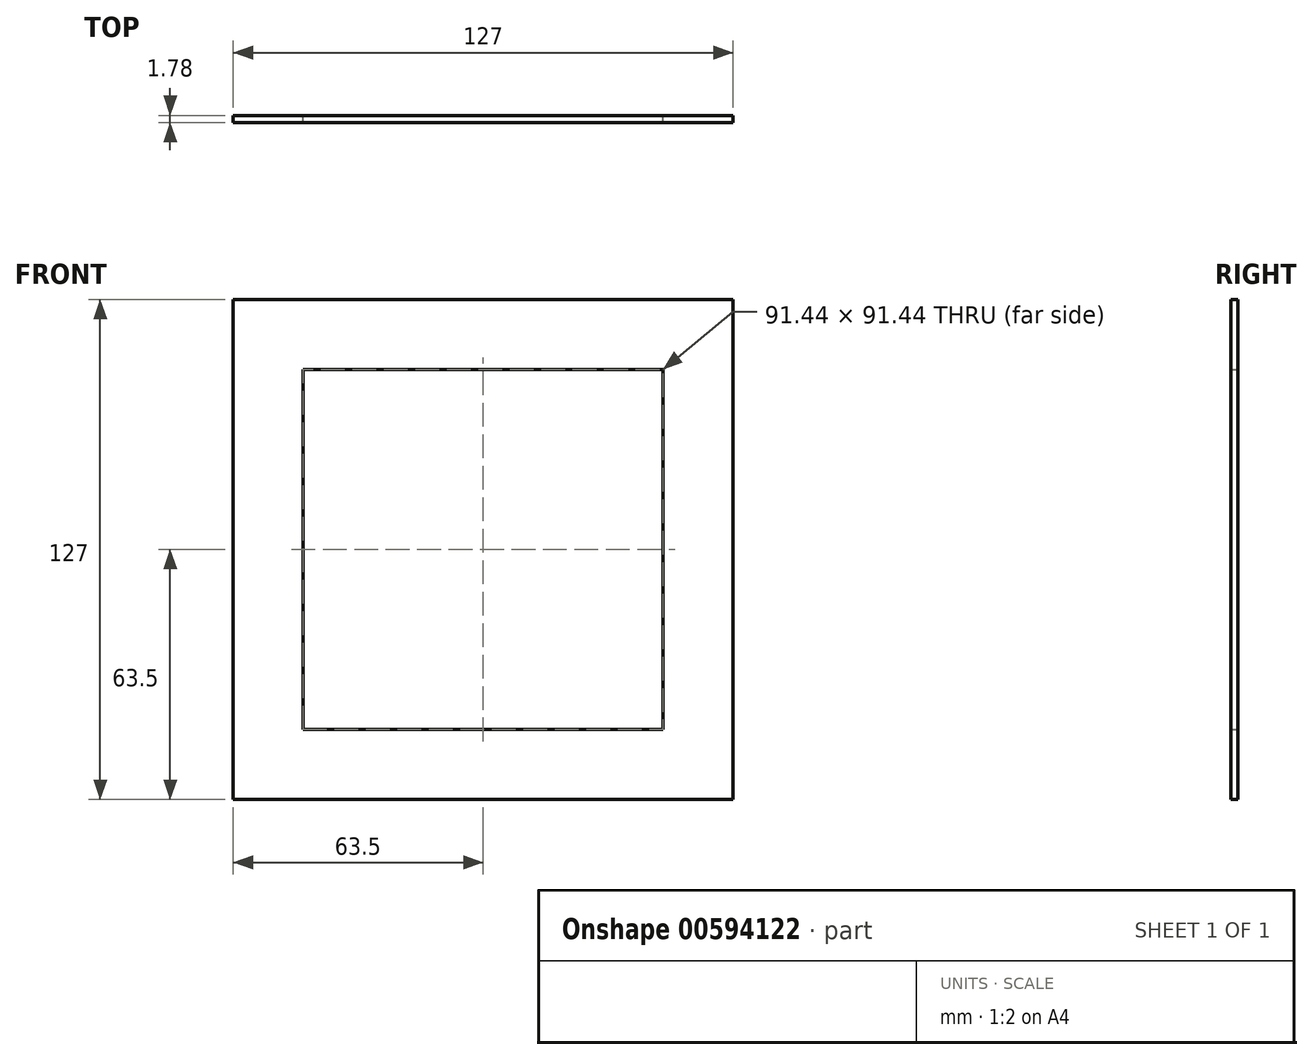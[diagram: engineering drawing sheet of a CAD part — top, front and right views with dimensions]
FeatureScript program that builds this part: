
annotation { "Feature Type Name" : "Feature", "Feature Type Description" : "" }
export const myFeature = defineFeature(function(context is Context, id is Id, definition is map)
    precondition{}
    {
        {
            var Q0;
            Q0=qCreatedBy(makeId("Front.planeOp"),FACE);
            var sketch = newSketch(context, id + "F0", { "sketchPlane" : qUnion([Q0])});
            skLineSegment(sketch, "E0.bottom", {"start": v(-63.5, -63.5) * mm, "end": v(63.5, -63.5) * mm});
            skLineSegment(sketch, "E0.top", {"start": v(-63.5, 63.5) * mm, "end": v(63.5, 63.5) * mm});
            skLineSegment(sketch, "E0.left", {"start": v(-63.5, -63.5) * mm, "end": v(-63.5, 63.5) * mm});
            skLineSegment(sketch, "E0.right", {"start": v(63.5, -63.5) * mm, "end": v(63.5, 63.5) * mm});
            skPoint(sketch, "E0.middle", {"position": v(0, 0) * mm});
            skLineSegment(sketch, "E1.bottom", {"start": v(-45.72, -45.72) * mm, "end": v(45.72, -45.72) * mm});
            skLineSegment(sketch, "E1.top", {"start": v(-45.72, 45.72) * mm, "end": v(45.72, 45.72) * mm});
            skLineSegment(sketch, "E1.left", {"start": v(-45.72, -45.72) * mm, "end": v(-45.72, 45.72) * mm});
            skLineSegment(sketch, "E1.right", {"start": v(45.72, -45.72) * mm, "end": v(45.72, 45.72) * mm});
            skSolve(sketch);
        }
        {
            var Q0;
            Q0 = qSketchRegion(id + "F0", true);
            extrude(context, id + "F1", {"entities" : qUnion([Q0]), "depth" : 1.78 * mm, "offsetDistance" : 25.4 * mm});
        }
    });
